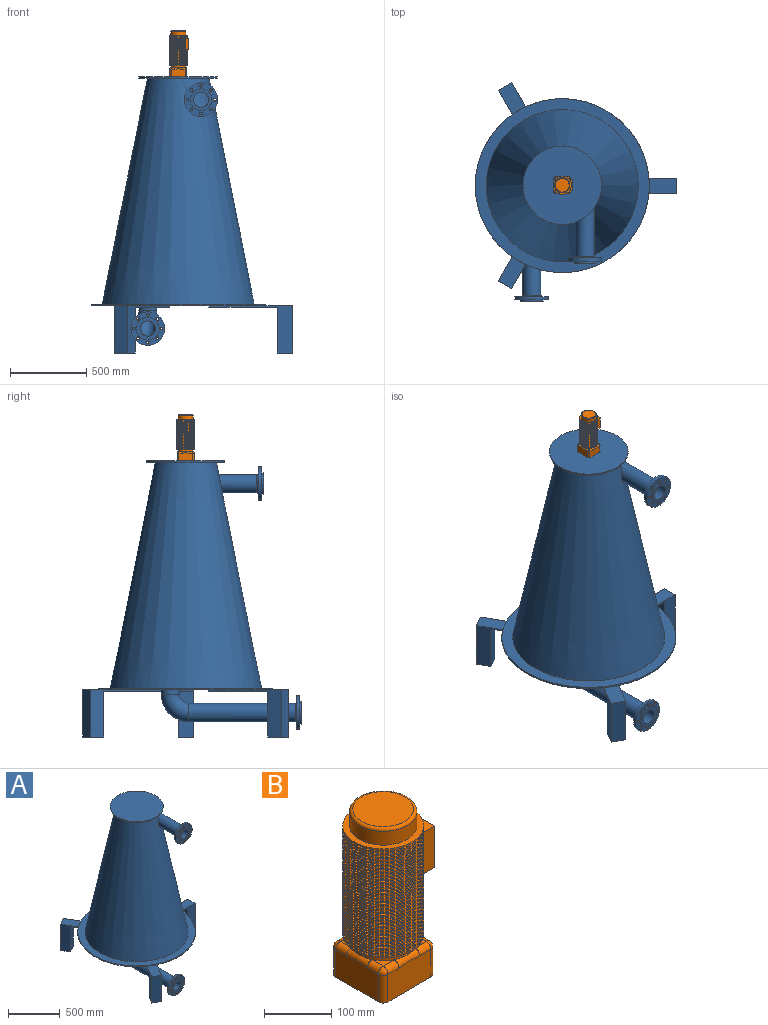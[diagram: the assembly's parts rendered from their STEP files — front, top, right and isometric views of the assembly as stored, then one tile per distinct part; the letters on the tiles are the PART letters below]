
ASSEMBLY  parts=2 mates=1
PART A: 69 faces, bbox 1320x1431.7x1810 mm
  f0: cylinder r=60mm len=374.41mm, axis (0,1,0), area 113555.1mm2, adj f1,f43
  f1: cone r=202mm half-angle=11.3deg, axis (0,0,-1), area 3302968.6mm2, adj f0,f3,f7
  f2: plane 1140x1137.8mm, normal (0,0,-1), area 898613.3mm2, adj f6,f9,f10,f12,f15,f16,f17,f21
  f3: plane 514.65x514.65mm, normal (0,0,-1), area 79835.6mm2, adj f1,f4
  f4: cylinder r=257.33mm len=514.65mm, axis (0,0,-1), area 16168.2mm2, adj f3,f5
  f5: plane 514.65x514.65mm, normal (0,0,1), area 208025.1mm2, adj f4
  f6: cylinder r=570mm len=1140mm, axis (0,0,-1), area 35814.2mm2, adj f2,f7,f8,f14,f20
  f7: plane 1140x1140mm, normal (0,0,1), area 241575.9mm2, adj f1,f6
  f8: plane 182.2x100mm, normal (0,0,1), area 18073.2mm2, adj f6,f10,f11,f12
  f9: plane 100x10mm, normal (-1,0,0), area 1000mm2, adj f2,f10,f12,f13
  f10: plane 550x310mm, normal (0,1,0), area 35500mm2, adj f2,f8,f9,f11,f13,f26,f27
  f11: plane 310x100mm, normal (1,0,0), area 31000mm2, adj f8,f10,f12,f27
  f12: plane 550x310mm, normal (0,-1,0), area 35500mm2, adj f2,f8,f9,f11,f13,f26,f27
  f13: plane 450x100mm, normal (0,0,-1), area 45000mm2, adj f9,f10,f12,f26
  f14: plane 207.79x177.7mm, normal (0,0,1), area 18073.2mm2, adj f6,f15,f17,f18
  f15: plane 476.31x310mm, normal (-0.87,0.5,0), area 35500mm2, adj f2,f14,f16,f18,f19,f28,f29
  f16: plane 86.6x50mm, normal (0.5,0.87,0), area 1000mm2, adj f2,f15,f17,f19
  f17: plane 476.31x310mm, normal (0.87,-0.5,0), area 35500mm2, adj f2,f14,f16,f18,f19,f28,f29
  f18: plane 310x86.6mm, normal (-0.5,-0.87,0), area 31000mm2, adj f14,f15,f17,f29
  f19: plane 439.71x311.6mm, normal (0,0,-1), area 45000mm2, adj f15,f16,f17,f28
  f20: plane 207.79x177.7mm, normal (0,0,1), area 18073.2mm2, adj f6,f21,f23,f24
  f21: plane 476.31x310mm, normal (0.87,0.5,0), area 35500mm2, adj f2,f20,f22,f24,f25,f30,f31
  f22: plane 86.6x50mm, normal (0.5,-0.87,0), area 1000mm2, adj f2,f21,f23,f25
  f23: plane 476.31x310mm, normal (-0.87,-0.5,0), area 35500mm2, adj f2,f20,f22,f24,f25,f30,f31
  f24: plane 310x86.6mm, normal (-0.5,0.87,0), area 31000mm2, adj f20,f21,f23,f31
  f25: plane 439.71x311.6mm, normal (0,0,-1), area 45000mm2, adj f21,f22,f23,f30
  f26: plane 300x100mm, normal (-1,0,0), area 30000mm2, adj f10,f12,f13,f27
  f27: plane 100x100mm, normal (0,0,-1), area 10000mm2, adj f10,f11,f12,f26
  f28: plane 300x86.6mm, normal (0.5,0.87,0), area 30000mm2, adj f15,f17,f19,f29
  f29: plane 136.6x136.6mm, normal (0,0,-1), area 10000mm2, adj f15,f17,f18,f28
  f30: plane 300x86.6mm, normal (0.5,-0.87,0), area 30000mm2, adj f21,f23,f25,f31
  f31: plane 136.6x136.6mm, normal (0,0,-1), area 10000mm2, adj f21,f23,f24,f30
  f32: cylinder r=9mm len=25mm, axis (0,-1,0), area 1413.7mm2, adj f41,f42
  f33: cylinder r=9mm len=25mm, axis (0,-1,0), area 1413.7mm2, adj f41,f42
  f34: cylinder r=9mm len=25mm, axis (0,-1,0), area 1413.7mm2, adj f41,f42
  f35: cylinder r=9mm len=25mm, axis (0,-1,0), area 1413.7mm2, adj f41,f42
  f36: cylinder r=9mm len=25mm, axis (0,-1,0), area 1413.7mm2, adj f41,f42
  f37: cylinder r=9mm len=25mm, axis (0,-1,0), area 1413.7mm2, adj f41,f42
  f38: cylinder r=9mm len=25mm, axis (0,-1,0), area 1413.7mm2, adj f41,f42
  f39: cylinder r=9mm len=25mm, axis (0,-1,0), area 1413.7mm2, adj f41,f42
  f40: cylinder r=110mm len=220mm, axis (0,-1,0), area 17278.8mm2, adj f41,f42
  f41: plane 220x220mm, normal (0,1,0), area 20583.7mm2, adj f32,f33,f34,f35,f36,f37,f38,f39
  f42: plane 220x220mm, normal (0,-1,0), area 20406.3mm2, adj f32,f33,f34,f35,f36,f37,f38,f39
  f43: torus R=70mm, axis (0,-1,0), area 6280.4mm2, adj f0,f41
  f44: cylinder r=70.4mm len=140.8mm, axis (0,1,0), area 4423.5mm2, adj f42,f45
  f45: plane 140.8x140.8mm, normal (0,-1,0), area 7717.2mm2, adj f44,f47
  f46: cone r=202mm half-angle=11.3deg, axis (0,0,-1), area 10991.4mm2, adj f47
  f47: cylinder r=50mm len=398.74mm, axis (0,1,0), area 107627.8mm2, adj f45,f46
  f48: cylinder r=60mm len=120mm, axis (0,0,-1), area 11309.7mm2, adj f2,f49
  f49: torus R=120mm, axis (-1,0,0), area 71061.2mm2, adj f48,f50
  f50: cylinder r=60mm len=697.17mm, axis (0,-1,0), area 262825.9mm2, adj f49,f68
  f51: cylinder r=9mm len=20mm, axis (0,-1,0), area 1131mm2, adj f60,f61
  f52: cylinder r=9mm len=20mm, axis (0,-1,0), area 1131mm2, adj f60,f61
  f53: cylinder r=9mm len=20mm, axis (0,-1,0), area 1131mm2, adj f60,f61
  f54: cylinder r=9mm len=20mm, axis (0,-1,0), area 1131mm2, adj f60,f61
  f55: cylinder r=9mm len=20mm, axis (0,-1,0), area 1131mm2, adj f60,f61
  f56: cylinder r=9mm len=20mm, axis (0,-1,0), area 1131mm2, adj f60,f61
  f57: cylinder r=9mm len=20mm, axis (0,-1,0), area 1131mm2, adj f60,f61
  f58: cylinder r=9mm len=20mm, axis (0,-1,0), area 1131mm2, adj f60,f61
  f59: cylinder r=110mm len=220mm, axis (0,-1,0), area 13823mm2, adj f60,f61
  f60: plane 220x220mm, normal (0,1,0), area 20583.7mm2, adj f51,f52,f53,f54,f55,f56,f57,f58
  f61: plane 220x220mm, normal (0,-1,0), area 18306.1mm2, adj f51,f52,f53,f54,f55,f56,f57,f58
  f62: cylinder r=75mm len=150mm, axis (0,1,0), area 4712.4mm2, adj f61,f63
  f63: plane 150x150mm, normal (0,-1,0), area 9817.5mm2, adj f62,f67
  f64: plane 100x100mm, normal (0,0,-1), area 7854mm2, adj f65
  f65: cylinder r=50mm len=100mm, axis (0,0,-1), area 9424.8mm2, adj f64,f66
  f66: torus R=120mm, axis (-1,0,0), area 59217.6mm2, adj f65,f67
  f67: cylinder r=50mm len=737.17mm, axis (0,-1,0), area 231587.9mm2, adj f63,f66
  f68: torus R=70mm, axis (0,-1,0), area 6280.4mm2, adj f50,f60
PART B: 197 faces, bbox 130x120x300 mm
  f0: plane 23.21x23.21mm, normal (0,0,1), area 208.3mm2, adj f164,f180,f185
  f1: plane 23.21x23.21mm, normal (0,0,1), area 208.3mm2, adj f164,f188,f189
  f2: plane 23.21x23.21mm, normal (0,0,1), area 208.3mm2, adj f164,f174,f175
  f3: cylinder r=50mm len=100mm, axis (0,0,-1), area 628.3mm2, adj f159,f161
  f4: cylinder r=50mm len=100mm, axis (0,0,-1), area 628.3mm2, adj f156,f158
  f5: cylinder r=50mm len=100mm, axis (0,0,-1), area 628.3mm2, adj f153,f155
  f6: cylinder r=50mm len=100mm, axis (0,0,-1), area 628.3mm2, adj f150,f152
  f7: cylinder r=50mm len=100mm, axis (0,0,-1), area 628.3mm2, adj f147,f149
  f8: cylinder r=50mm len=100mm, axis (0,0,-1), area 628.3mm2, adj f144,f146
  f9: cylinder r=50mm len=100mm, axis (0,0,-1), area 628.3mm2, adj f141,f143
  f10: cylinder r=50mm len=100mm, axis (0,0,-1), area 628.3mm2, adj f138,f140
  f11: cylinder r=50mm len=100mm, axis (0,0,-1), area 628.3mm2, adj f135,f137
  f12: cylinder r=50mm len=100mm, axis (0,0,-1), area 628.3mm2, adj f132,f134
  f13: cylinder r=50mm len=100mm, axis (0,0,-1), area 628.3mm2, adj f129,f131
  f14: cylinder r=50mm len=100mm, axis (0,0,-1), area 628.3mm2, adj f126,f128
  f15: cylinder r=50mm len=100mm, axis (0,0,-1), area 628.3mm2, adj f123,f125
  f16: cylinder r=50mm len=100mm, axis (0,0,-1), area 628.3mm2, adj f120,f122
  f17: cylinder r=50mm len=100mm, axis (0,0,-1), area 628.3mm2, adj f117,f119
  f18: cylinder r=50mm len=100mm, axis (0,0,-1), area 628.3mm2, adj f114,f116
  f19: cylinder r=50mm len=100mm, axis (0,0,-1), area 628.3mm2, adj f111,f113
  f20: cylinder r=50mm len=100mm, axis (0,0,-1), area 628.3mm2, adj f108,f110
  f21: cylinder r=50mm len=100mm, axis (0,0,-1), area 628.3mm2, adj f105,f107
  f22: cylinder r=50mm len=100mm, axis (0,0,-1), area 628.3mm2, adj f102,f104
  f23: cylinder r=50mm len=100mm, axis (0,0,-1), area 628.3mm2, adj f99,f101
  f24: cylinder r=50mm len=100mm, axis (0,0,-1), area 458.7mm2, adj f96,f98,f192,f194
  f25: cylinder r=50mm len=100mm, axis (0,0,-1), area 458.7mm2, adj f93,f95,f192,f194
  f26: cylinder r=50mm len=100mm, axis (0,0,-1), area 458.7mm2, adj f90,f92,f192,f194
  f27: cylinder r=50mm len=100mm, axis (0,0,-1), area 458.7mm2, adj f87,f89,f192,f194
  f28: cylinder r=50mm len=100mm, axis (0,0,-1), area 458.7mm2, adj f84,f86,f192,f194
  f29: cylinder r=50mm len=100mm, axis (0,0,-1), area 458.7mm2, adj f81,f83,f192,f194
  f30: cylinder r=50mm len=100mm, axis (0,0,-1), area 458.7mm2, adj f78,f80,f192,f194
  f31: cylinder r=50mm len=100mm, axis (0,0,-1), area 458.7mm2, adj f75,f77,f192,f194
  f32: cylinder r=50mm len=100mm, axis (0,0,-1), area 458.7mm2, adj f72,f74,f192,f194
  f33: cylinder r=50mm len=100mm, axis (0,0,-1), area 458.7mm2, adj f69,f71,f192,f194
  f34: cylinder r=50mm len=100mm, axis (0,0,-1), area 458.7mm2, adj f66,f68,f192,f194
  f35: cylinder r=50mm len=100mm, axis (0,0,-1), area 458.7mm2, adj f63,f65,f192,f194
  f36: cylinder r=50mm len=100mm, axis (0,0,-1), area 458.7mm2, adj f60,f62,f192,f194
  f37: cylinder r=50mm len=100mm, axis (0,0,-1), area 458.7mm2, adj f57,f59,f192,f194
  f38: cylinder r=50mm len=100mm, axis (0,0,-1), area 458.7mm2, adj f54,f56,f192,f194
  f39: cylinder r=50mm len=100mm, axis (0,0,-1), area 628.3mm2, adj f51,f53
  f40: cylinder r=50mm len=100mm, axis (0,0,-1), area 628.3mm2, adj f48,f50
  f41: cylinder r=50mm len=100mm, axis (0,0,-1), area 628.3mm2, adj f43,f47
  f42: plane 120x120mm, normal (0,0,1), area 3455.8mm2, adj f44,f46
  f43: plane 120x120mm, normal (0,0,-1), area 3455.8mm2, adj f41,f44
  f44: cylinder r=60mm len=120mm, axis (0,0,1), area 1131mm2, adj f42,f43
  f45: plane 90x90mm, normal (0,0,1), area 6361.7mm2, adj f165
  f46: cylinder r=50mm len=100mm, axis (0,0,-1), area 7854mm2, adj f42,f165
  f47: plane 120x120mm, normal (0,0,1), area 3455.8mm2, adj f41,f49
  f48: plane 120x120mm, normal (0,0,-1), area 3455.8mm2, adj f40,f49
  f49: cylinder r=60mm len=120mm, axis (0,0,1), area 1131mm2, adj f47,f48
  f50: plane 120x120mm, normal (0,0,1), area 3455.8mm2, adj f40,f52
  f51: plane 120x120mm, normal (0,0,-1), area 3455.8mm2, adj f39,f52
  f52: cylinder r=60mm len=120mm, axis (0,0,1), area 1131mm2, adj f50,f51
  f53: plane 120x120mm, normal (0,0,1), area 3455.8mm2, adj f39,f55
  f54: plane 120x106.84mm, normal (0,0,-1), area 2629.2mm2, adj f38,f55,f192,f194
  f55: cylinder r=60mm len=120mm, axis (0,0,1), area 1054.7mm2, adj f53,f54,f192,f193,f194
  f56: plane 120x106.84mm, normal (0,0,1), area 2629.2mm2, adj f38,f58,f192,f194
  f57: plane 120x106.84mm, normal (0,0,-1), area 2629.2mm2, adj f37,f58,f192,f194
  f58: cylinder r=60mm len=120mm, axis (0,0,1), area 887.9mm2, adj f56,f57,f192,f194
  f59: plane 120x106.84mm, normal (0,0,1), area 2629.2mm2, adj f37,f61,f192,f194
  f60: plane 120x106.84mm, normal (0,0,-1), area 2629.2mm2, adj f36,f61,f192,f194
  f61: cylinder r=60mm len=120mm, axis (0,0,1), area 887.9mm2, adj f59,f60,f192,f194
  f62: plane 120x106.84mm, normal (0,0,1), area 2629.2mm2, adj f36,f64,f192,f194
  f63: plane 120x106.84mm, normal (0,0,-1), area 2629.2mm2, adj f35,f64,f192,f194
  f64: cylinder r=60mm len=120mm, axis (0,0,1), area 887.9mm2, adj f62,f63,f192,f194
  f65: plane 120x106.84mm, normal (0,0,1), area 2629.2mm2, adj f35,f67,f192,f194
  f66: plane 120x106.84mm, normal (0,0,-1), area 2629.2mm2, adj f34,f67,f192,f194
  f67: cylinder r=60mm len=120mm, axis (0,0,1), area 887.9mm2, adj f65,f66,f192,f194
  f68: plane 120x106.84mm, normal (0,0,1), area 2629.2mm2, adj f34,f70,f192,f194
  f69: plane 120x106.84mm, normal (0,0,-1), area 2629.2mm2, adj f33,f70,f192,f194
  f70: cylinder r=60mm len=120mm, axis (0,0,1), area 887.9mm2, adj f68,f69,f192,f194
  f71: plane 120x106.84mm, normal (0,0,1), area 2629.2mm2, adj f33,f73,f192,f194
  f72: plane 120x106.84mm, normal (0,0,-1), area 2629.2mm2, adj f32,f73,f192,f194
  f73: cylinder r=60mm len=120mm, axis (0,0,1), area 887.9mm2, adj f71,f72,f192,f194
  f74: plane 120x106.84mm, normal (0,0,1), area 2629.2mm2, adj f32,f76,f192,f194
  f75: plane 120x106.84mm, normal (0,0,-1), area 2629.2mm2, adj f31,f76,f192,f194
  f76: cylinder r=60mm len=120mm, axis (0,0,1), area 887.9mm2, adj f74,f75,f192,f194
  f77: plane 120x106.84mm, normal (0,0,1), area 2629.2mm2, adj f31,f79,f192,f194
  f78: plane 120x106.84mm, normal (0,0,-1), area 2629.2mm2, adj f30,f79,f192,f194
  f79: cylinder r=60mm len=120mm, axis (0,0,1), area 887.9mm2, adj f77,f78,f192,f194
  f80: plane 120x106.84mm, normal (0,0,1), area 2629.2mm2, adj f30,f82,f192,f194
  f81: plane 120x106.84mm, normal (0,0,-1), area 2629.2mm2, adj f29,f82,f192,f194
  f82: cylinder r=60mm len=120mm, axis (0,0,1), area 887.9mm2, adj f80,f81,f192,f194
  f83: plane 120x106.84mm, normal (0,0,1), area 2629.2mm2, adj f29,f85,f192,f194
  f84: plane 120x106.84mm, normal (0,0,-1), area 2629.2mm2, adj f28,f85,f192,f194
  f85: cylinder r=60mm len=120mm, axis (0,0,1), area 887.9mm2, adj f83,f84,f192,f194
  f86: plane 120x106.84mm, normal (0,0,1), area 2629.2mm2, adj f28,f88,f192,f194
  f87: plane 120x106.84mm, normal (0,0,-1), area 2629.2mm2, adj f27,f88,f192,f194
  f88: cylinder r=60mm len=120mm, axis (0,0,1), area 887.9mm2, adj f86,f87,f192,f194
  f89: plane 120x106.84mm, normal (0,0,1), area 2629.2mm2, adj f27,f91,f192,f194
  f90: plane 120x106.84mm, normal (0,0,-1), area 2629.2mm2, adj f26,f91,f192,f194
  f91: cylinder r=60mm len=120mm, axis (0,0,1), area 887.9mm2, adj f89,f90,f192,f194
  f92: plane 120x106.84mm, normal (0,0,1), area 2629.2mm2, adj f26,f94,f192,f194
  f93: plane 120x106.84mm, normal (0,0,-1), area 2629.2mm2, adj f25,f94,f192,f194
  f94: cylinder r=60mm len=120mm, axis (0,0,1), area 887.9mm2, adj f92,f93,f192,f194
  f95: plane 120x106.84mm, normal (0,0,1), area 2629.2mm2, adj f25,f97,f192,f194
  f96: plane 120x106.84mm, normal (0,0,-1), area 2629.2mm2, adj f24,f97,f192,f194
  f97: cylinder r=60mm len=120mm, axis (0,0,1), area 887.9mm2, adj f95,f96,f192,f194
  f98: plane 120x106.84mm, normal (0,0,1), area 2629.2mm2, adj f24,f100,f192,f194
  f99: plane 120x120mm, normal (0,0,-1), area 3455.8mm2, adj f23,f100
  f100: cylinder r=60mm len=120mm, axis (0,0,1), area 964.2mm2, adj f98,f99,f192,f194,f195
  f101: plane 120x120mm, normal (0,0,1), area 3455.8mm2, adj f23,f103
  f102: plane 120x120mm, normal (0,0,-1), area 3455.8mm2, adj f22,f103
  f103: cylinder r=60mm len=120mm, axis (0,0,1), area 1131mm2, adj f101,f102
  f104: plane 120x120mm, normal (0,0,1), area 3455.8mm2, adj f22,f106
  f105: plane 120x120mm, normal (0,0,-1), area 3455.8mm2, adj f21,f106
  f106: cylinder r=60mm len=120mm, axis (0,0,1), area 1131mm2, adj f104,f105
  f107: plane 120x120mm, normal (0,0,1), area 3455.8mm2, adj f21,f109
  f108: plane 120x120mm, normal (0,0,-1), area 3455.8mm2, adj f20,f109
  f109: cylinder r=60mm len=120mm, axis (0,0,1), area 1131mm2, adj f107,f108
  f110: plane 120x120mm, normal (0,0,1), area 3455.8mm2, adj f20,f112
  f111: plane 120x120mm, normal (0,0,-1), area 3455.8mm2, adj f19,f112
  f112: cylinder r=60mm len=120mm, axis (0,0,1), area 1131mm2, adj f110,f111
  f113: plane 120x120mm, normal (0,0,1), area 3455.8mm2, adj f19,f115
  f114: plane 120x120mm, normal (0,0,-1), area 3455.8mm2, adj f18,f115
  f115: cylinder r=60mm len=120mm, axis (0,0,1), area 1131mm2, adj f113,f114
  f116: plane 120x120mm, normal (0,0,1), area 3455.8mm2, adj f18,f118
  f117: plane 120x120mm, normal (0,0,-1), area 3455.8mm2, adj f17,f118
  f118: cylinder r=60mm len=120mm, axis (0,0,1), area 1131mm2, adj f116,f117
  f119: plane 120x120mm, normal (0,0,1), area 3455.8mm2, adj f17,f121
  f120: plane 120x120mm, normal (0,0,-1), area 3455.8mm2, adj f16,f121
  f121: cylinder r=60mm len=120mm, axis (0,0,1), area 1131mm2, adj f119,f120
  f122: plane 120x120mm, normal (0,0,1), area 3455.8mm2, adj f16,f124
  f123: plane 120x120mm, normal (0,0,-1), area 3455.8mm2, adj f15,f124
  f124: cylinder r=60mm len=120mm, axis (0,0,1), area 1131mm2, adj f122,f123
  f125: plane 120x120mm, normal (0,0,1), area 3455.8mm2, adj f15,f127
  f126: plane 120x120mm, normal (0,0,-1), area 3455.8mm2, adj f14,f127
  f127: cylinder r=60mm len=120mm, axis (0,0,1), area 1131mm2, adj f125,f126
  f128: plane 120x120mm, normal (0,0,1), area 3455.8mm2, adj f14,f130
  f129: plane 120x120mm, normal (0,0,-1), area 3455.8mm2, adj f13,f130
  f130: cylinder r=60mm len=120mm, axis (0,0,1), area 1131mm2, adj f128,f129
  f131: plane 120x120mm, normal (0,0,1), area 3455.8mm2, adj f13,f133
  f132: plane 120x120mm, normal (0,0,-1), area 3455.8mm2, adj f12,f133
  f133: cylinder r=60mm len=120mm, axis (0,0,1), area 1131mm2, adj f131,f132
  f134: plane 120x120mm, normal (0,0,1), area 3455.8mm2, adj f12,f136
  f135: plane 120x120mm, normal (0,0,-1), area 3455.8mm2, adj f11,f136
  f136: cylinder r=60mm len=120mm, axis (0,0,1), area 1131mm2, adj f134,f135
  f137: plane 120x120mm, normal (0,0,1), area 3455.8mm2, adj f11,f139
  f138: plane 120x120mm, normal (0,0,-1), area 3455.8mm2, adj f10,f139
  f139: cylinder r=60mm len=120mm, axis (0,0,1), area 1131mm2, adj f137,f138
  f140: plane 120x120mm, normal (0,0,1), area 3455.8mm2, adj f10,f142
  f141: plane 120x120mm, normal (0,0,-1), area 3455.8mm2, adj f9,f142
  f142: cylinder r=60mm len=120mm, axis (0,0,1), area 1131mm2, adj f140,f141
  f143: plane 120x120mm, normal (0,0,1), area 3455.8mm2, adj f9,f145
  f144: plane 120x120mm, normal (0,0,-1), area 3455.8mm2, adj f8,f145
  f145: cylinder r=60mm len=120mm, axis (0,0,1), area 1131mm2, adj f143,f144
  f146: plane 120x120mm, normal (0,0,1), area 3455.8mm2, adj f8,f148
  f147: plane 120x120mm, normal (0,0,-1), area 3455.8mm2, adj f7,f148
  f148: cylinder r=60mm len=120mm, axis (0,0,1), area 1131mm2, adj f146,f147
  f149: plane 120x120mm, normal (0,0,1), area 3455.8mm2, adj f7,f151
  f150: plane 120x120mm, normal (0,0,-1), area 3455.8mm2, adj f6,f151
  f151: cylinder r=60mm len=120mm, axis (0,0,1), area 1131mm2, adj f149,f150
  f152: plane 120x120mm, normal (0,0,1), area 3455.8mm2, adj f6,f154
  f153: plane 120x120mm, normal (0,0,-1), area 3455.8mm2, adj f5,f154
  f154: cylinder r=60mm len=120mm, axis (0,0,1), area 1131mm2, adj f152,f153
  f155: plane 120x120mm, normal (0,0,1), area 3455.8mm2, adj f5,f157
  f156: plane 120x120mm, normal (0,0,-1), area 3455.8mm2, adj f4,f157
  f157: cylinder r=60mm len=120mm, axis (0,0,1), area 1131mm2, adj f155,f156
  f158: plane 120x120mm, normal (0,0,1), area 3455.8mm2, adj f4,f160
  f159: plane 120x120mm, normal (0,0,-1), area 3455.8mm2, adj f3,f160
  f160: cylinder r=60mm len=120mm, axis (0,0,1), area 1131mm2, adj f158,f159
  f161: plane 120x120mm, normal (0,0,1), area 3455.8mm2, adj f3,f163
  f162: plane 120x120mm, normal (0,0,-1), area 3455.8mm2, adj f163,f164
  f163: cylinder r=60mm len=120mm, axis (0,0,1), area 1131mm2, adj f161,f162
  f164: cylinder r=50mm len=100mm, axis (0,0,-1), area 3769.9mm2, adj f0,f1,f2,f162,f170,f176,f177,f186
  f165: torus R=45mm, axis (0,0,-1), area 2377.7mm2, adj f45,f46
  f166: plane 90x51.34mm, normal (0,1,0), area 4530.1mm2, adj f171,f178,f184,f186,f188,f191
  f167: plane 90x51.34mm, normal (-1,0,0), area 4530.1mm2, adj f171,f181,f185,f187,f189,f191
  f168: plane 90x51.34mm, normal (0,-1,0), area 4530.1mm2, adj f171,f172,f175,f177,f180,f181
  f169: plane 90x51.34mm, normal (1,0,0), area 4530.1mm2, adj f171,f172,f174,f176,f178,f179
  f170: plane 23.21x23.21mm, normal (0,0,1), area 208.3mm2, adj f164,f179,f184
  f171: plane 110x110mm, normal (0,0,-1), area 12014.2mm2, adj f166,f167,f168,f169,f172,f178,f181,f191
  f172: cylinder r=10mm len=50mm, axis (0,0,-1), area 785.4mm2, adj f168,f169,f171,f173
  f173: sphere r=10mm, area 157.1mm2, adj f172,f174,f175
  f174: cylinder r=10mm len=23.21mm, axis (0,-1,0), area 364.5mm2, adj f2,f169,f173,f176
  f175: cylinder r=10mm len=23.21mm, axis (-1,0,0), area 364.5mm2, adj f2,f168,f173,f177
  f176: bspline ~48.45x11.27mm, area 534.3mm2, adj f164,f169,f174,f179
  f177: bspline ~48.45x11.27mm, area 534.3mm2, adj f164,f168,f175,f180
  f178: cylinder r=10mm len=50mm, axis (0,0,1), area 785.4mm2, adj f166,f169,f171,f182
  f179: cylinder r=10mm len=23.21mm, axis (0,-1,0), area 364.5mm2, adj f169,f170,f176,f182
  f180: cylinder r=10mm len=23.21mm, axis (-1,0,0), area 364.5mm2, adj f0,f168,f177,f183
  f181: cylinder r=10mm len=50mm, axis (0,0,1), area 785.4mm2, adj f167,f168,f171,f183
  f182: sphere r=10mm, area 157.1mm2, adj f178,f179,f184
  f183: sphere r=10mm, area 157.1mm2, adj f180,f181,f185
  f184: cylinder r=10mm len=23.21mm, axis (1,0,0), area 364.5mm2, adj f166,f170,f182,f186
  f185: cylinder r=10mm len=23.21mm, axis (0,1,0), area 364.5mm2, adj f0,f167,f183,f187
  f186: bspline ~48.45x11.27mm, area 534.3mm2, adj f164,f166,f184,f188
  f187: bspline ~48.45x11.27mm, area 534.3mm2, adj f164,f167,f185,f189
  f188: cylinder r=10mm len=23.21mm, axis (1,0,0), area 364.5mm2, adj f1,f166,f186,f190
  f189: cylinder r=10mm len=23.21mm, axis (0,1,0), area 364.5mm2, adj f1,f167,f187,f190
  f190: sphere r=10mm, area 157.1mm2, adj f188,f189,f191
  f191: cylinder r=10mm len=50mm, axis (0,0,-1), area 785.4mm2, adj f166,f167,f171,f190
  f192: plane 75x36.93mm, normal (0,1,0), area 2150.2mm2, adj f24,f25,f26,f27,f28,f29,f30,f31
  f193: plane 75x23.16mm, normal (0,0,1), area 1063.1mm2, adj f55,f192,f194,f196
  f194: plane 75x36.93mm, normal (0,-1,0), area 2150.2mm2, adj f24,f25,f26,f27,f28,f29,f30,f31
  f195: plane 75x23.16mm, normal (0,0,-1), area 1063.1mm2, adj f100,f192,f194,f196
  f196: plane 75x75mm, normal (1,0,0), area 5625mm2, adj f192,f193,f194,f195
PLACE A t=(-93,42.88,-590.08)mm
PLACE B t=(-93,42.88,909.92)mm
MATE planar B.f3 <-> A.f1  axis (0,0,-1) through (-93,42.88,909.92)mm
